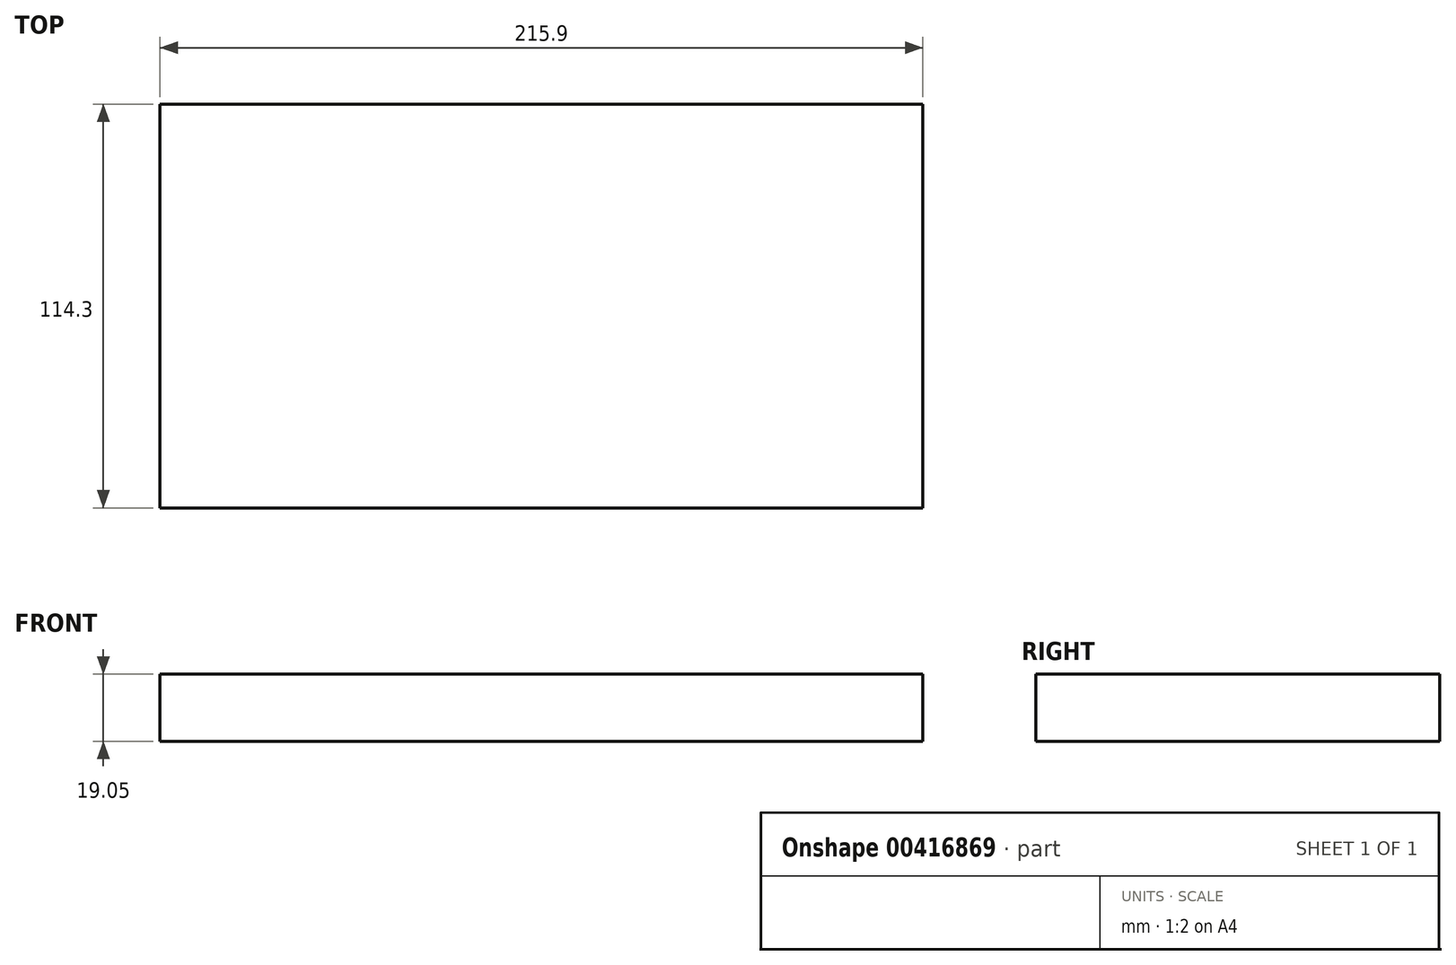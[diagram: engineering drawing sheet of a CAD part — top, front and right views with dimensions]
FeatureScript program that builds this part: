
annotation { "Feature Type Name" : "Feature", "Feature Type Description" : "" }
export const myFeature = defineFeature(function(context is Context, id is Id, definition is map)
    precondition{}
    {
        {
            var Q0;
            Q0=qCreatedBy(makeId("Top.planeOp"),FACE);
            var sketch = newSketch(context, id + "F0", { "sketchPlane" : qUnion([Q0])});
            skLineSegment(sketch, "E0.bottom", {"start": v(-107.95, 57.15) * mm, "end": v(107.95, 57.15) * mm});
            skLineSegment(sketch, "E0.top", {"start": v(-107.95, -57.15) * mm, "end": v(107.95, -57.15) * mm});
            skLineSegment(sketch, "E0.left", {"start": v(-107.95, 57.15) * mm, "end": v(-107.95, -57.15) * mm});
            skLineSegment(sketch, "E0.right", {"start": v(107.95, 57.15) * mm, "end": v(107.95, -57.15) * mm});
            skPoint(sketch, "E0.middle", {"position": v(0, 0) * mm});
            skSolve(sketch);
        }
        {
            var Q0;
            Q0 = qSketchRegion(id + "F0", true);
            extrude(context, id + "F1", {"entities" : qUnion([Q0]), "depth" : 19.05 * mm});
        }
    });
